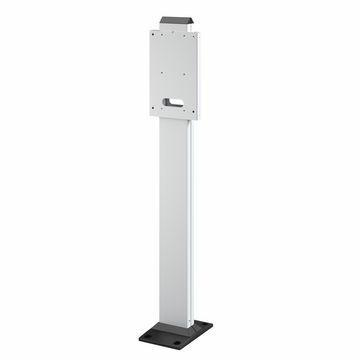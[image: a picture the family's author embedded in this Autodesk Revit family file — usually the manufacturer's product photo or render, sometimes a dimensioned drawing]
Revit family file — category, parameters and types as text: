
# Revit family: Building-ElectricalVehicleCharging-GEWISS-JOINON-ICON_1-SIDED-FLOOR-MOUNT-SUPPORT
name_source: partatom
category: Apparecchi elettrici
units: mm (PartAtom-declared; Revit-internal decimal feet)

## family parameters
Condiviso = No
Host = Superficie
Mantenere orientamento annotazione = Sì
Punto di calcolo locali = Sì
Quota connettore circolare = Usa diametro
Taglio con vuoti quando caricato = No
Tipo di parte = Normale

## types (1)
- GWJ8102 - I-CON - ONE-SIDED FLOOR-MOUNTING SUPPORT
    BLOCCO = B=C
    Catalogue = E-MOBILITY
    Description: = I-CON floor-mounting support - single-sided
    Descrizione = I-CON - ONE-SIDED FLOOR-MOUNTING SUPPORT
    EAN code = 8034035071379
    Electrocod = 2242
    FORMULA = 1000 mm  [stored 3.28084 ft]
    IDF = 419b6614-7cdf-4001-b9f8-4c2d8e728900
    IDT = 9d8fff42-0005-4008-88f3-94fb88b800ce
    Immagine tipo = ICON_SUPP_MONO.jpg
    L = 155 mm  [stored 0.50853 ft]
    Modello = GWJ8102
    N.poli = 1
    POMELLO = bianco
    PRESA = Giallo
    Produttore = GEWISS S.p.A.
    Prospetto di default = 1219 mm
    STRUTTURA = RAL - 7035
    STRUTTURA ALTA = blue
    Spostamento_S = 1500 mm  [stored 4.92126 ft]
    Suitable for = WallBox I-CON
    Technical sheet = https://www.gewiss.com
    URL = https://www.gewiss.com
    VETRO = Vetro
    Version file RFA = 19.4
    Voltaggio = 0 V
    W = 115 mm  [stored 0.377297 ft]

note: [stored X ft] marks values corroborated as IEEE doubles in the binary element streams (Revit-internal decimal feet)
